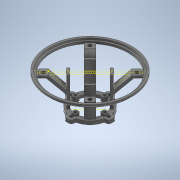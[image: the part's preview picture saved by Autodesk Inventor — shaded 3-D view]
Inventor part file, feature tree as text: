
AUTODESK INVENTOR PART (.ipt)
format: ipt  version: 2020 (Build 240168000, 168)  size: 770,048 bytes
history: native  units: mm
features: projected_geometry x29, sketch x17, extrude x11, other x6, pattern_circular x1, sweep x1, fillet x1
ambient origin geometry x8: Origin, YZ Plane, XZ Plane, XY Plane, X Axis, Y Axis, Z Axis, Center Point
bodies: Body1 (feature_tree)
feature tree (66):
  other  "Твердое тело1"
  sketch  "Эскиз1"
  extrude  "Выдавливание1"  Depth=44.0mm
  extrude  "Выдавливание2"  Depth=3.8mm
  sketch  "Эскиз3"
  extrude  "Выдавливание4"  Depth=40.0mm TaperAngle=360.0deg
  pattern_circular  "Круговой массив1"  [2 undecoded]
  other  "РабПлоскость2"
  sketch  "Эскиз5"
  other  "РабПлоскость1"
  sketch  "Эскиз6"
  sketch  "Эскиз7"
  extrude  "Выдавливание6"  Depth=4.5mm
  sketch  "Эскиз8"
  extrude  "Выдавливание7"  Depth=3.0mm
  sketch  "Эскиз9"
  other  "РабПлоскость3"
  sketch  "Эскиз10"
  sweep  "Сдвиг1"
  extrude  "Выдавливание8"  Depth=1.0mm
  extrude  "Выдавливание9"  TaperAngle=45.0deg  [1 undecoded]
  sketch  "Эскиз14"
  other  "РабПлоскость4"
  sketch  "Эскиз15"
  extrude  "Выдавливание10"  TaperAngle=135.0deg  [1 undecoded]
  extrude  "Выдавливание11"  Depth=34.0mm
  other  "РабПлоскость5"
  sketch  "Эскиз16"
  extrude  "Выдавливание13"  Depth=4.0mm TaperAngle=0.0deg
  extrude  "Выдавливание12"  Depth=3.0mm
  fillet  "Сопряжение1"  [1 undecoded]
  sketch  "Эскиз2"
  sketch  "Эскиз4"
  projected_geometry  "Спроецированная петля1"
  projected_geometry  "Спроецированная петля2"
  projected_geometry  "Спроецированная петля3"
  projected_geometry  "Спроецированная петля4"
  projected_geometry  "Спроецированная петля5"
  projected_geometry  "Спроецированная петля6"
  projected_geometry  "Спроецированная петля7"
  projected_geometry  "Спроецированная петля8"
  projected_geometry  "Спроецированная петля9"
  projected_geometry  "Спроецированная петля10"
  projected_geometry  "Спроецированная петля11"
  projected_geometry  "Спроецированная петля12"
  projected_geometry  "Спроецированная петля13"
  projected_geometry  "Спроецированная петля14"
  projected_geometry  "Спроецированная петля15"
  projected_geometry  "Спроецированная петля16"
  projected_geometry  "Спроецированная петля17"
  projected_geometry  "Спроецированная петля18"
  projected_geometry  "Спроецированная петля19"
  projected_geometry  "Спроецированная петля20"
  sketch  "Эскиз11"
  projected_geometry  "Спроецированная петля21"
  projected_geometry  "Спроецированная петля22"
  projected_geometry  "Спроецированная петля23"
  sketch  "3D эскиз1"
  sketch  "Эскиз12"
  sketch  "Эскиз13"
  projected_geometry  "Спроецированная петля24"
  projected_geometry  "Спроецированная петля25"
  projected_geometry  "Спроецированная петля26"
  projected_geometry  "Спроецированная петля27"
  projected_geometry  "Спроецированная петля28"
  projected_geometry  "Спроецированная петля29"
note: 5 required parameter values undecoded (feature->parameter linkage not recoverable at this tier; creation-order binding heuristic only, values carry confidence <= 0.55)
